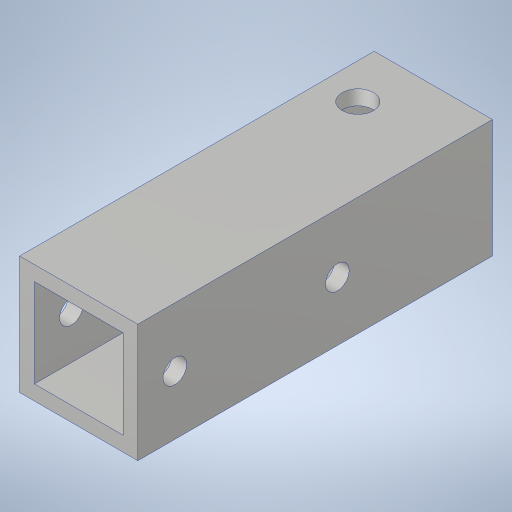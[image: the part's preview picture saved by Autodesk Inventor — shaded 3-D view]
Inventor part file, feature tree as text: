
AUTODESK INVENTOR PART (.ipt)
format: ipt  version: 2023.4 (Build 274418000, 418)  size: 229,376 bytes
history: native  units: in
note: dims shown in document units (in); Inventor stores cm internally (conversion verified against a paired STEP export)
features: hole x2, sketch x2, extrude x1
ambient origin geometry x8: Origin, YZ Plane, XZ Plane, XY Plane, X Axis, Y Axis, Z Axis, Center Point
bodies: Solid1 (feature_tree)
feature tree (5):
  extrude  "Extrusion1"  Depth=1.375in
  hole  "Hole2"  [1 undecoded]
  hole  "Hole3"  [1 undecoded]
  sketch  "Sketch3"  dims[d4=0.0in d22=1.375in]
  sketch  "Sketch4"  dims[d23=0.201in d24=0.75in d25=0.385in d26=0.25in d27=0.5635in d28=1.0in d29=0.8108in d30=0.266in d31=0.75in d32=0.762in d33=0.25in d34=0.5635in d35=1.0in d36=0.8108in d37=0.313in d38=0.4375in d39=0.3in]
note: 2 required parameter values undecoded (feature->parameter linkage not recoverable at this tier; creation-order binding heuristic only, values carry confidence <= 0.55)
